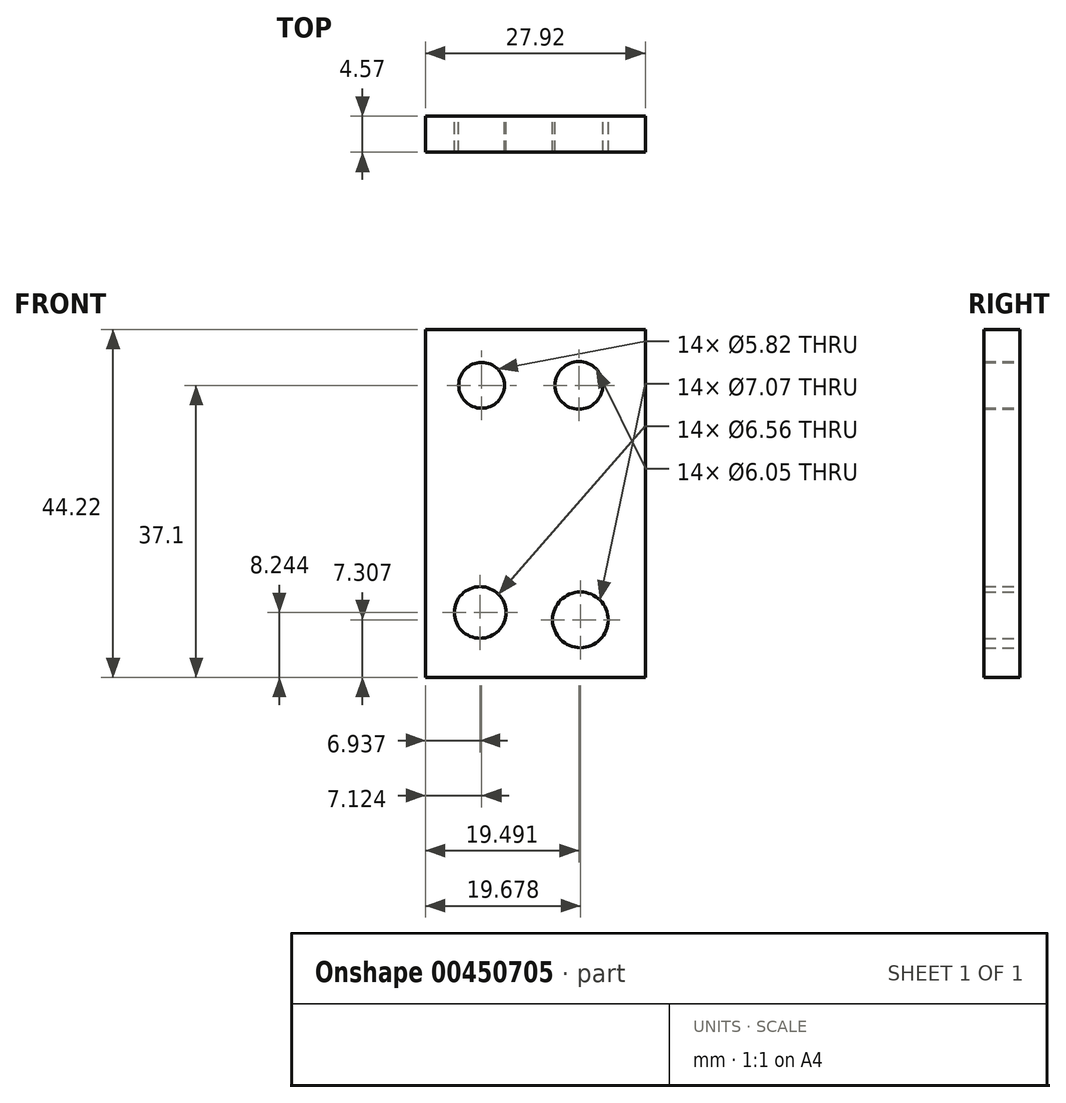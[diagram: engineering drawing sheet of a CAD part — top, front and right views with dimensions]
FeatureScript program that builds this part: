
annotation { "Feature Type Name" : "Feature", "Feature Type Description" : "" }
export const myFeature = defineFeature(function(context is Context, id is Id, definition is map)
    precondition{}
    {
        {
            var Q0;
            Q0=qCreatedBy(makeId("Front.planeOp"),FACE);
            var sketch = newSketch(context, id + "F0", { "sketchPlane" : qUnion([Q0])});
            skLineSegment(sketch, "E0", {"start": v(-17.43, 18.55) * mm, "end": v(-17.43, -25.67) * mm});
            skLineSegment(sketch, "E1", {"start": v(-17.43, -25.67) * mm, "end": v(10.5, -25.67) * mm});
            skLineSegment(sketch, "E2", {"start": v(10.5, -25.67) * mm, "end": v(10.5, 18.55) * mm});
            skLineSegment(sketch, "E3", {"start": v(10.5, 18.55) * mm, "end": v(-17.43, 18.55) * mm});
            skSolve(sketch);
        }
        {
            var Q0;
            Q0=makeQuery(id+"F0.imprint","IMPRINT",FACE,{"disambiguationData":[TD([[makeQuery(id+"F0.imprint","IMPRINT",EDGE,{"derivedFrom":sQuery(id+"F0.wireOp",EDGE,"E0")}),1.0]])]});
            extrude(context, id + "F1", {"entities" : qUnion([Q0]), "depth" : 4.57 * mm});
        }
        {
            var Q0;
            Q0=qCreatedBy(makeId("Front.planeOp"),FACE);
            var sketch = newSketch(context, id + "F2", { "sketchPlane" : qUnion([Q0])});
            skCircle(sketch, "E4", {"center": v(-10.3, 11.43) * mm, "radius": 2.9 * mm});
            skCircle(sketch, "E5", {"center": v(2.06, 11.43) * mm, "radius": 3.03 * mm});
            skCircle(sketch, "E6", {"center": v(-10.5, -17.43) * mm, "radius": 3.28 * mm});
            skCircle(sketch, "E7", {"center": v(2.25, -18.36) * mm, "radius": 3.54 * mm});
            skSolve(sketch);
        }
        {
            var Q0;
            Q0=makeQuery(id+"F2.imprint","IMPRINT",FACE,{"disambiguationData":[TD([[makeQuery(id+"F2.imprint","IMPRINT",EDGE,{"derivedFrom":sQuery(id+"F2.wireOp",EDGE,"E4")}),1.0]])]});
            var Q1;
            Q1=makeQuery(id+"F2.imprint","IMPRINT",FACE,{"disambiguationData":[TD([[makeQuery(id+"F2.imprint","IMPRINT",EDGE,{"derivedFrom":sQuery(id+"F2.wireOp",EDGE,"E7")}),1.0]])]});
            var Q2;
            Q2=makeQuery(id+"F2.imprint","IMPRINT",FACE,{"disambiguationData":[TD([[makeQuery(id+"F2.imprint","IMPRINT",EDGE,{"derivedFrom":sQuery(id+"F2.wireOp",EDGE,"E6")}),1.0]])]});
            var Q3;
            Q3=makeQuery(id+"F2.imprint","IMPRINT",FACE,{"disambiguationData":[TD([[makeQuery(id+"F2.imprint","IMPRINT",EDGE,{"derivedFrom":sQuery(id+"F2.wireOp",EDGE,"E5")}),1.0]])]});
            extrude(context, id + "F3", {"entities" : qUnion([Q0, Q1, Q2, Q3]), "operationType" : NewBodyOperationType.REMOVE, "depth" : 25.4 * mm});
        }
    });
